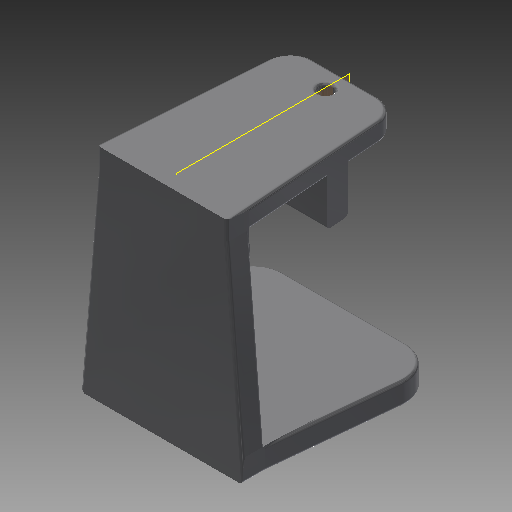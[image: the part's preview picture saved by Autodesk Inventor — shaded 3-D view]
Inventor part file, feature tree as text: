
AUTODESK INVENTOR PART (.ipt)
format: ipt  version: 2018 (Build 220112000, 112)  size: 285,184 bytes
history: native  units: mm
features: extrude x4, sketch x4, projected_geometry x3, fillet x2, plane x1
ambient origin geometry x8: Origin, YZ Plane, XZ Plane, XY Plane, X Axis, Y Axis, Z Axis, Center Point
bodies: Solid1 (feature_tree)
feature tree (14):
  extrude  "Extrusion1"  Depth=10.0mm
  plane  "Work Plane1"
  extrude  "Extrusion2"  Depth=10.0mm
  extrude  "Extrusion3"  Depth=10.0mm TaperAngle=0.0deg
  extrude  "Extrusion4"  Depth=0.5mm
  fillet  "Fillet2"  Radius=3.5mm
  fillet  "Fillet5"  Radius=30.0mm
  sketch  "Sketch1"  dims[d0=3.0mm d1=0.0mm d3=10.0mm]
  sketch  "Sketch3"  dims[d4=5.0mm d6=10.0mm]
  sketch  "Sketch5"  dims[d7=3.5mm d8=10.0mm d9=0.0mm]
  sketch  "Sketch6"  dims[d10=28.0mm d11=25.0mm d12=3.5mm d13=0.0mm d14=30.0mm d15=15.0mm d16=25.0mm d17=3.5mm d18=0.0mm d19=5.0mm d22=0.5mm]
  projected_geometry  "Project Cut Edges1"
  projected_geometry  "Project Cut Edges2"
  projected_geometry  "Project Cut Edges3"
